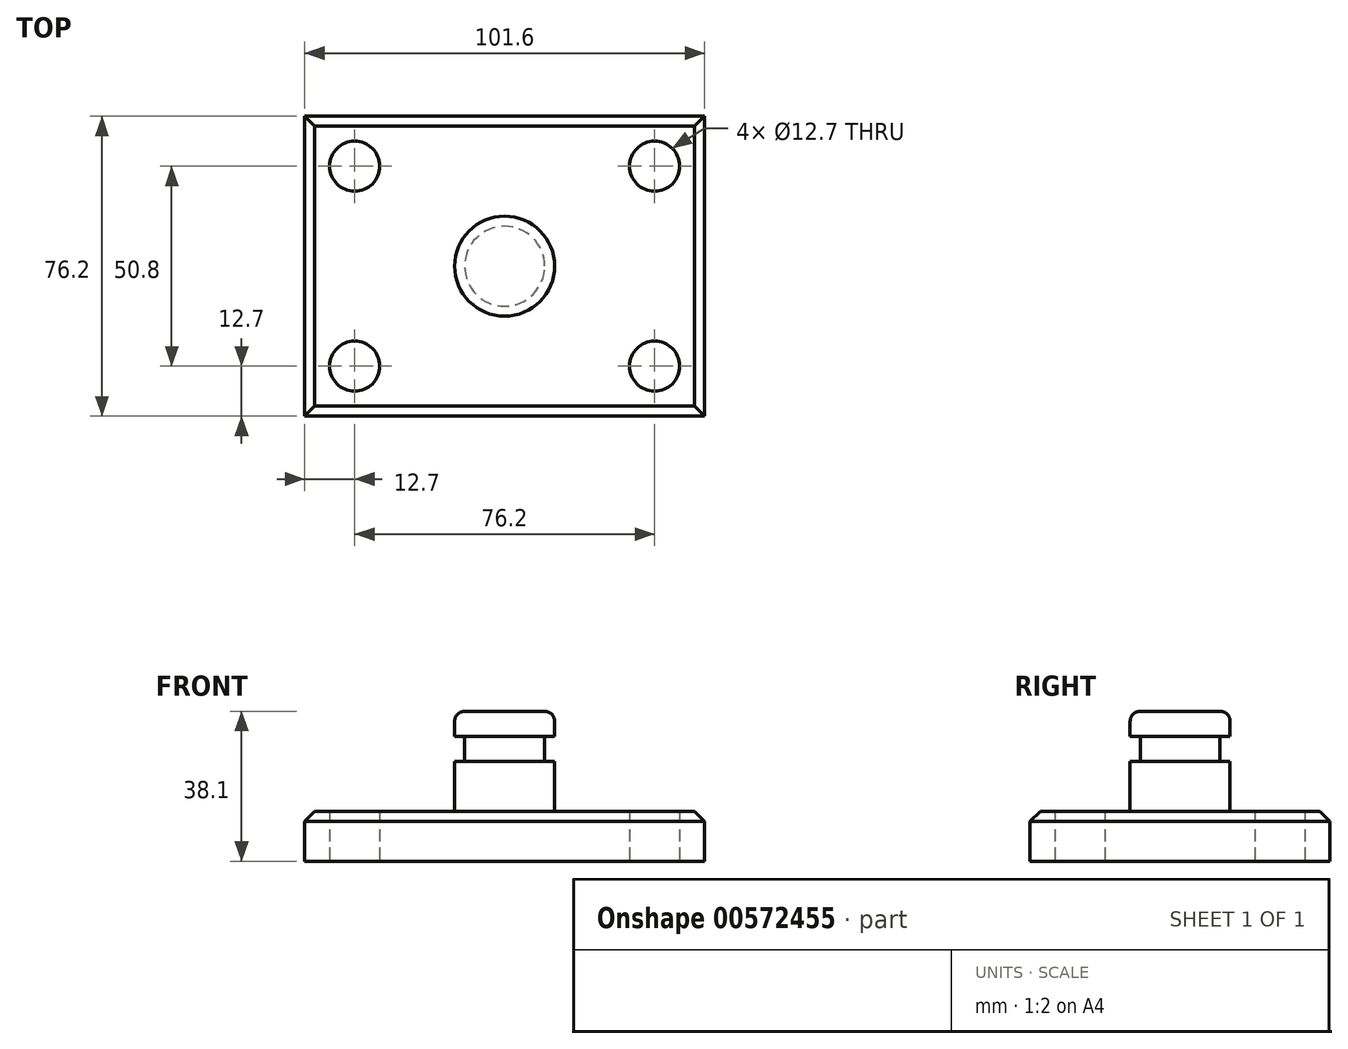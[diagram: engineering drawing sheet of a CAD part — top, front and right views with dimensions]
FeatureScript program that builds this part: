
annotation { "Feature Type Name" : "Feature", "Feature Type Description" : "" }
export const myFeature = defineFeature(function(context is Context, id is Id, definition is map)
    precondition{}
    {
        {
            var Q0;
            Q0=qCreatedBy(makeId("Top.planeOp"),FACE);
            var sketch = newSketch(context, id + "F0", { "sketchPlane" : qUnion([Q0])});
            skLineSegment(sketch, "E0.bottom", {"start": v(-50.8, 38.1) * mm, "end": v(50.8, 38.1) * mm});
            skLineSegment(sketch, "E0.top", {"start": v(-50.8, -38.1) * mm, "end": v(50.8, -38.1) * mm});
            skLineSegment(sketch, "E0.left", {"start": v(-50.8, 38.1) * mm, "end": v(-50.8, -38.1) * mm});
            skLineSegment(sketch, "E0.right", {"start": v(50.8, 38.1) * mm, "end": v(50.8, -38.1) * mm});
            skPoint(sketch, "E0.middle", {"position": v(0, 0) * mm});
            skSolve(sketch);
        }
        {
            var Q0;
            Q0 = qSketchRegion(id + "F0", true);
            extrude(context, id + "F1", {"entities" : qUnion([Q0]), "depth" : 12.7 * mm, "offsetDistance" : 25.4 * mm});
        }
        {
            var Q0;
            Q0=makeQuery(id+"F1.opExtrude","CAP_FACE",FACE,{"disambiguationData":[OSD([sQuery(id+"F0.wireOp",EDGE,"E0.bottom"),sQuery(id+"F0.wireOp",EDGE,"E0.top"),sQuery(id+"F0.wireOp",EDGE,"E0.left"),sQuery(id+"F0.wireOp",EDGE,"E0.right")])],"isStart":true});
            var sketch = newSketch(context, id + "F2", { "sketchPlane" : qUnion([Q0])});
            skCircle(sketch, "E1", {"center": v(-38.1, 25.4) * mm, "radius": 6.35 * mm});
            skCircle(sketch, "E2", {"center": v(38.1, 25.4) * mm, "radius": 6.35 * mm});
            skCircle(sketch, "E3", {"center": v(-38.1, -25.4) * mm, "radius": 6.35 * mm});
            skCircle(sketch, "E4", {"center": v(38.1, -25.4) * mm, "radius": 6.35 * mm});
            skSolve(sketch);
        }
        {
            var Q0;
            Q0=makeQuery(id+"F2.imprint","IMPRINT",FACE,{"disambiguationData":[TD([[makeQuery(id+"F2.imprint","IMPRINT",EDGE,{"derivedFrom":sQuery(id+"F2.wireOp",EDGE,"E2")}),1.0]])]});
            var Q1;
            Q1=makeQuery(id+"F2.imprint","IMPRINT",FACE,{"disambiguationData":[TD([[makeQuery(id+"F2.imprint","IMPRINT",EDGE,{"derivedFrom":sQuery(id+"F2.wireOp",EDGE,"E4")}),1.0]])]});
            var Q2;
            Q2=makeQuery(id+"F2.imprint","IMPRINT",FACE,{"disambiguationData":[TD([[makeQuery(id+"F2.imprint","IMPRINT",EDGE,{"derivedFrom":sQuery(id+"F2.wireOp",EDGE,"E3")}),1.0]])]});
            var Q3;
            Q3=makeQuery(id+"F2.imprint","IMPRINT",FACE,{"disambiguationData":[TD([[makeQuery(id+"F2.imprint","IMPRINT",EDGE,{"derivedFrom":sQuery(id+"F2.wireOp",EDGE,"E1")}),1.0]])]});
            extrude(context, id + "F3", {"entities" : qUnion([Q0, Q1, Q2, Q3]), "operationType" : NewBodyOperationType.REMOVE, "endBound" : BoundingType.THROUGH_ALL, "oppositeDirection" : true, "depth" : 25.4 * mm, "offsetDistance" : 25.4 * mm});
        }
        {
            var Q0;
            Q0=qCreatedBy(makeId("Front.planeOp"),FACE);
            var sketch = newSketch(context, id + "F4", { "sketchPlane" : qUnion([Q0])});
            skLineSegment(sketch, "E5.bottom", {"start": v(0, 38.1) * mm, "end": v(12.7, 38.1) * mm});
            skLineSegment(sketch, "E5.top", {"start": v(0, 12.7) * mm, "end": v(12.7, 12.7) * mm});
            skLineSegment(sketch, "E5.left", {"start": v(0, 38.1) * mm, "end": v(0, 12.7) * mm});
            skLineSegment(sketch, "E5.right", {"start": v(12.7, 38.1) * mm, "end": v(12.7, 12.7) * mm});
            skSolve(sketch);
        }
        {
            var Q0;
            Q0=makeQuery(id+"F4.imprint","IMPRINT",FACE,{"disambiguationData":[TD([[makeQuery(id+"F4.imprint","IMPRINT",EDGE,{"derivedFrom":sQuery(id+"F4.wireOp",EDGE,"E5.bottom")}),-1.0]])]});
            var Q1;
            Q1=sQuery(id+"F4.wireOp",EDGE,"E5.left");
            revolve(context, id + "F5", {"operationType" : NewBodyOperationType.ADD, "entities" : qUnion([Q0]), "axis" : qUnion([Q1]), "revolveType" : RevolveType.FULL});
        }
        {
            var Q0;
            Q0=qCreatedBy(makeId("Front.planeOp"),FACE);
            var sketch = newSketch(context, id + "F6", { "sketchPlane" : qUnion([Q0])});
            skLineSegment(sketch, "E6.bottom", {"start": v(10.16, 31.75) * mm, "end": v(14.88, 31.75) * mm});
            skLineSegment(sketch, "E6.top", {"start": v(10.16, 25.4) * mm, "end": v(14.88, 25.4) * mm});
            skLineSegment(sketch, "E6.left", {"start": v(10.16, 31.75) * mm, "end": v(10.16, 25.4) * mm});
            skLineSegment(sketch, "E6.right", {"start": v(14.88, 31.75) * mm, "end": v(14.88, 25.4) * mm});
            skSolve(sketch);
        }
        {
            var Q0;
            Q0=makeQuery(id+"F6.imprint","IMPRINT",FACE,{"disambiguationData":[TD([[makeQuery(id+"F6.imprint","IMPRINT",EDGE,{"derivedFrom":sQuery(id+"F6.wireOp",EDGE,"E6.bottom")}),-1.0]])]});
            var Q1;
            Q1=makeQuery(id+"F5.opRevolve","SWEPT_FACE",FACE,{"disambiguationData":[OSD([sQuery(id+"F4.wireOp",EDGE,"E5.right")])]});
            revolve(context, id + "F7", {"operationType" : NewBodyOperationType.REMOVE, "entities" : qUnion([Q0]), "axis" : qUnion([Q1]), "revolveType" : RevolveType.FULL, "oppositeDirection" : true});
        }
        {
            var Q0;
            Q0=makeQuery(id+"F5.opRevolve","SWEPT_EDGE",EDGE,{"disambiguationData":[OSD([sQuery(id+"F4.wireOp",EDGE,"E5.bottom"),sQuery(id+"F4.wireOp",EDGE,"E5.right")])]});
            var Q1;
            Q1=makeQuery(id+"F5.opRevolve","SWEPT_EDGE",EDGE,{"disambiguationData":[OSD([sQuery(id+"F4.wireOp",EDGE,"E5.top"),sQuery(id+"F4.wireOp",EDGE,"E5.right")])]});
            fillet(context, id + "F8", {"entities" : qUnion([Q0, Q1]), "radius" : 2.54 * mm, "tangentPropagation" : true, "allowEdgeOverflow" : false});
        }
        {
            var Q0;
            Q0=makeQuery(id+"F1.opExtrude","CAP_EDGE",EDGE,{"disambiguationData":[OSD([sQuery(id+"F0.wireOp",EDGE,"E0.left")])],"isStart":false});
            var Q1;
            Q1=makeQuery(id+"F1.opExtrude","CAP_EDGE",EDGE,{"disambiguationData":[OSD([sQuery(id+"F0.wireOp",EDGE,"E0.top")])],"isStart":false});
            var Q2;
            Q2=makeQuery(id+"F1.opExtrude","CAP_EDGE",EDGE,{"disambiguationData":[OSD([sQuery(id+"F0.wireOp",EDGE,"E0.right")])],"isStart":false});
            var Q3;
            Q3=makeQuery(id+"F1.opExtrude","CAP_EDGE",EDGE,{"disambiguationData":[OSD([sQuery(id+"F0.wireOp",EDGE,"E0.bottom")])],"isStart":false});
            chamfer(context, id + "F9", {"entities" : qUnion([Q0, Q1, Q2, Q3]), "width" : 2.54 * mm, "tangentPropagation" : true});
        }
    });
